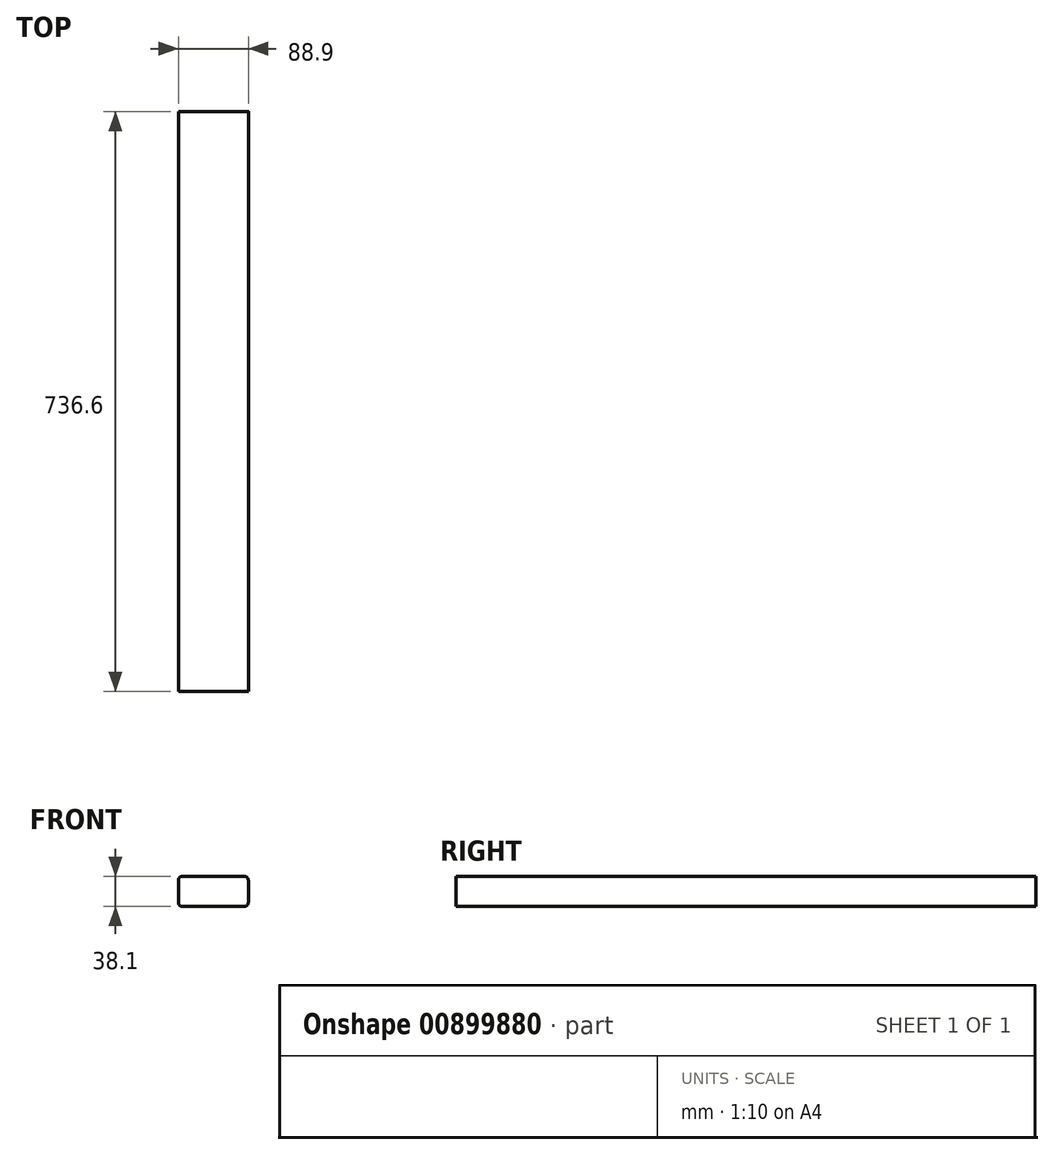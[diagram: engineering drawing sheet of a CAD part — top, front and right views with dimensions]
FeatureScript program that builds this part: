
annotation { "Feature Type Name" : "Feature", "Feature Type Description" : "" }
export const myFeature = defineFeature(function(context is Context, id is Id, definition is map)
    precondition{}
    {
        {
            var Q0;
            Q0=qCreatedBy(makeId("Front.planeOp"),FACE);
            var sketch = newSketch(context, id + "F0", { "sketchPlane" : qUnion([Q0])});
            skLineSegment(sketch, "E0.bottom", {"start": v(0, 0) * mm, "end": v(88.9, 0) * mm});
            skLineSegment(sketch, "E0.top", {"start": v(0, 38.1) * mm, "end": v(88.9, 38.1) * mm});
            skLineSegment(sketch, "E0.left", {"start": v(0, 0) * mm, "end": v(0, 38.1) * mm});
            skLineSegment(sketch, "E0.right", {"start": v(88.9, 0) * mm, "end": v(88.9, 38.1) * mm});
            skSolve(sketch);
        }
        {
            var Q0;
            Q0=qSketchRegion(id+"F0",true);
            extrude(context, id + "F1", {"entities" : qUnion([Q0]), "depth" : 736.6 * mm, "offsetDistance" : 25.4 * mm});
        }
        {
            var Q0;
            Q0=makeQuery(id+"F1.opExtrude","SWEPT_EDGE",EDGE,{"disambiguationData":[OSD([sQuery(id+"F0.wireOp",EDGE,"E0.bottom"),sQuery(id+"F0.wireOp",EDGE,"E0.right")])]});
            var Q1;
            Q1=makeQuery(id+"F1.opExtrude","SWEPT_EDGE",EDGE,{"disambiguationData":[OSD([sQuery(id+"F0.wireOp",EDGE,"E0.bottom"),sQuery(id+"F0.wireOp",EDGE,"E0.left")])]});
            var Q2;
            Q2=makeQuery(id+"F1.opExtrude","SWEPT_EDGE",EDGE,{"disambiguationData":[OSD([sQuery(id+"F0.wireOp",EDGE,"E0.top"),sQuery(id+"F0.wireOp",EDGE,"E0.right")])]});
            var Q3;
            Q3=makeQuery(id+"F1.opExtrude","SWEPT_EDGE",EDGE,{"disambiguationData":[OSD([sQuery(id+"F0.wireOp",EDGE,"E0.top"),sQuery(id+"F0.wireOp",EDGE,"E0.left")])]});
            fillet(context, id + "F2", {"entities" : qUnion([Q0, Q1, Q2, Q3]), "radius" : 5.08 * mm, "tangentPropagation" : true, "allowEdgeOverflow" : false});
        }
    });
